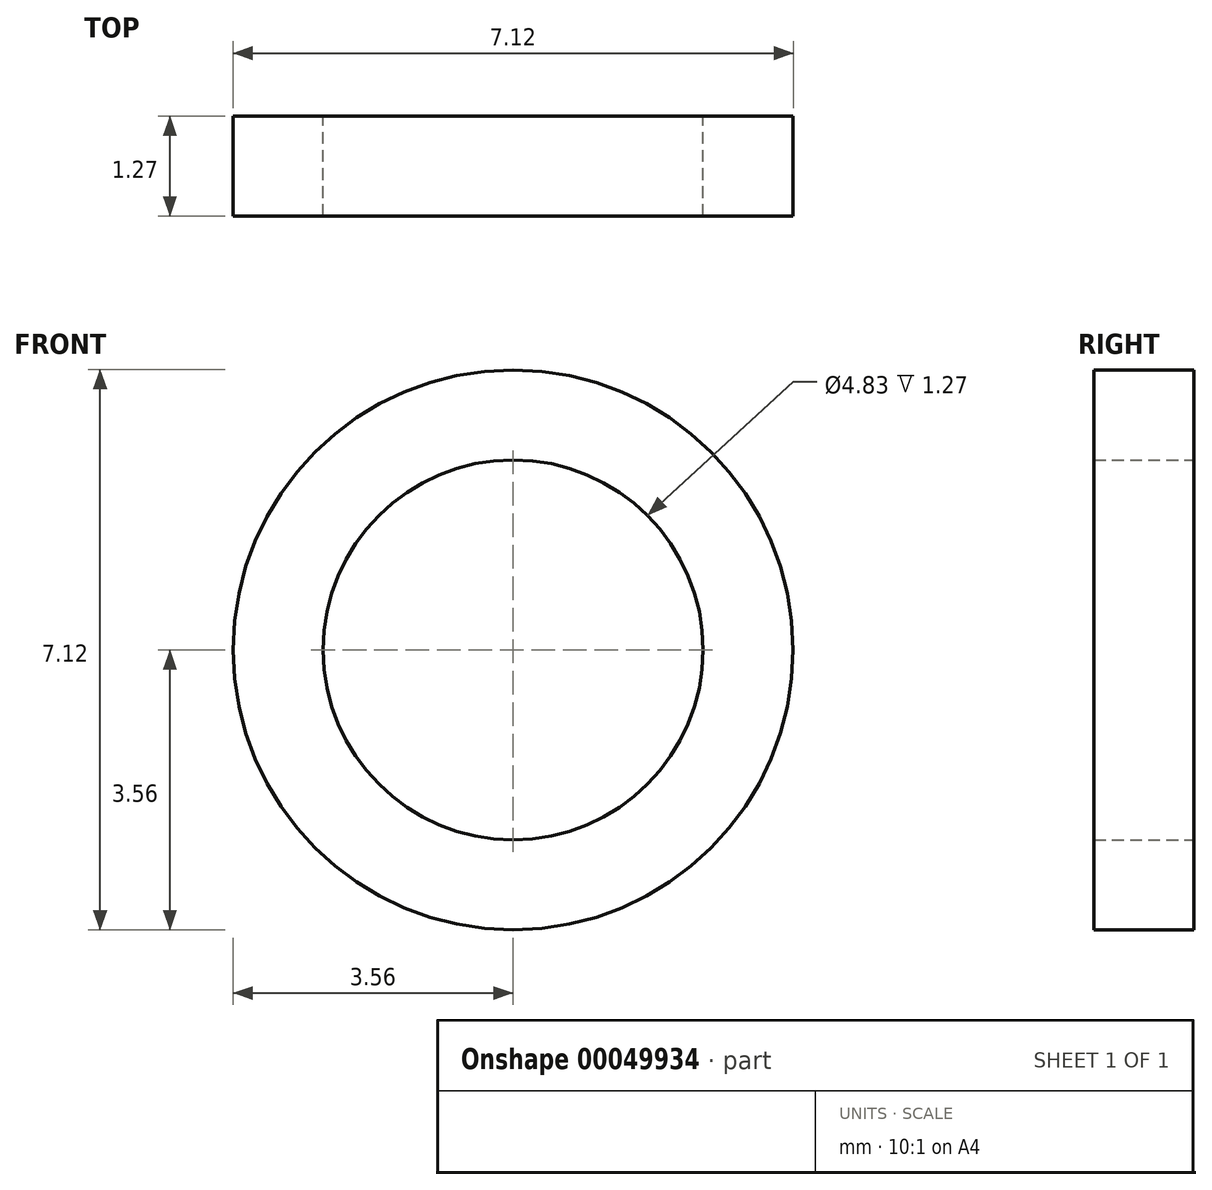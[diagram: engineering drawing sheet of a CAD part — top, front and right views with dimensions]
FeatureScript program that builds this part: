
annotation { "Feature Type Name" : "Feature", "Feature Type Description" : "" }
export const myFeature = defineFeature(function(context is Context, id is Id, definition is map)
    precondition{}
    {
        {
            var Q0;
            Q0=qCreatedBy(makeId("Front.planeOp"),FACE);
            var sketch = newSketch(context, id + "F0", { "sketchPlane" : qUnion([Q0])});
            skCircle(sketch, "E0", {"center": v(0, 0) * mm, "radius": 3.56 * mm});
            skLineSegment(sketch, "E1", {"start": v(0, 0) * mm, "end": v(3.56, 0) * mm});
            skLineSegment(sketch, "E2", {"start": v(0, 0) * mm, "end": v(-2.41, 0) * mm});
            skCircle(sketch, "E3", {"center": v(0, 0) * mm, "radius": 2.41 * mm});
            skSolve(sketch);
        }
        {
            var Q0;
            Q0 = qSketchRegion(id + "F0", true);
            extrude(context, id + "F1", {"entities" : qUnion([Q0]), "depth" : 1.27 * mm});
        }
    });
